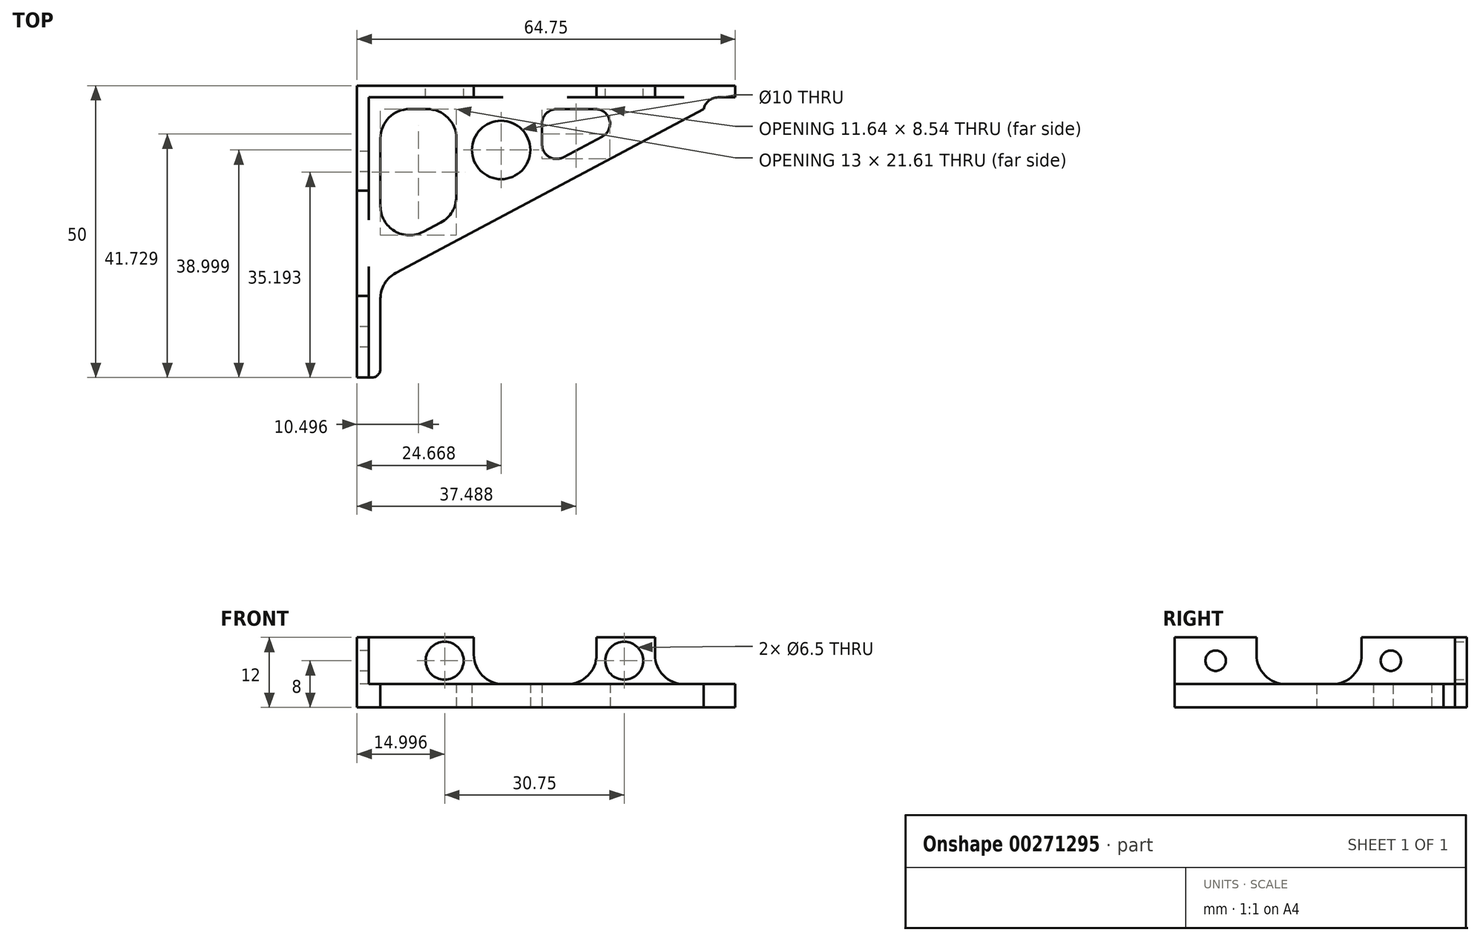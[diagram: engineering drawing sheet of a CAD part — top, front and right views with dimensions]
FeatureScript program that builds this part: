
annotation { "Feature Type Name" : "Feature", "Feature Type Description" : "" }
export const myFeature = defineFeature(function(context is Context, id is Id, definition is map)
    precondition{}
    {
        {
            var Q0;
            Q0=qCreatedBy(makeId("Top.planeOp"),FACE);
            var sketch = newSketch(context, id + "F0", { "sketchPlane" : qUnion([Q0])});
            skLineSegment(sketch, "E0.left", {"start": v(-24.04, 11.1) * mm, "end": v(-24.04, -13.83) * mm});
            skLineSegment(sketch, "E1", {"start": v(-28.04, 15.1) * mm, "end": v(-28.04, -34.9) * mm});
            skLineSegment(sketch, "E2", {"start": v(36.7, 15.1) * mm, "end": v(-28.04, 15.1) * mm});
            skLineSegment(sketch, "E3", {"start": v(-28.04, -34.9) * mm, "end": v(-24.04, -34.9) * mm});
            skLineSegment(sketch, "E4", {"start": v(-24.04, -34.9) * mm, "end": v(-24.04, -18.37) * mm});
            skLineSegment(sketch, "E5", {"start": v(-24.04, 11.1) * mm, "end": v(31.3, 11.1) * mm});
            skLineSegment(sketch, "E6", {"start": v(36.7, 15.1) * mm, "end": v(36.7, 13.1) * mm});
            skLineSegment(sketch, "E7", {"start": v(36.7, 13.1) * mm, "end": v(31.3, 13.1) * mm});
            skLineSegment(sketch, "E8", {"start": v(31.3, 13.1) * mm, "end": v(31.3, 11.1) * mm});
            skLineSegment(sketch, "E9", {"start": v(-24.04, -18.37) * mm, "end": v(31.3, 11.1) * mm});
            skLineSegment(sketch, "E10", {"start": v(-24.04, -13.83) * mm, "end": v(22.8, 11.1) * mm});
            skCircle(sketch, "E11", {"center": v(-3.37, 4.1) * mm, "radius": 5 * mm});
            skLineSegment(sketch, "E12", {"start": v(-11.04, 11.1) * mm, "end": v(-11.04, -6.91) * mm});
            skLineSegment(sketch, "E13", {"start": v(3.63, 11.1) * mm, "end": v(3.63, 0.9) * mm});
            skSolve(sketch);
        }
        {
            var Q0;
            {var subQ7=sQuery(id+"F0.wireOp",EDGE,"E0.left");Q0=makeQuery(id+"F0.imprint","IMPRINT",FACE,{"disambiguationData":[TD([[makeQuery(id+"F0.imprint","IMPRINT",EDGE,{"derivedFrom":subQ7}),-1.0]])]});}
            var Q1;
            Q1=makeQuery(id+"F0.imprint","IMPRINT",FACE,{"disambiguationData":[TD([[makeQuery(id+"F0.imprint","IMPRINT",EDGE,{"derivedFrom":sQuery(id+"F0.wireOp",EDGE,"E11")}),-1.0]])]});
            extrude(context, id + "F1", {"entities" : qUnion([Q0, Q1]), "depth" : 4 * mm});
        }
        {
            var Q0;
            Q0=qCreatedBy(makeId("Top.planeOp"),FACE);
            var sketch = newSketch(context, id + "F2", { "sketchPlane" : qUnion([Q0])});
            skLineSegment(sketch, "E14.bottom", {"start": v(-28.04, 15.1) * mm, "end": v(-26.04, 15.1) * mm});
            skLineSegment(sketch, "E14.top", {"start": v(-28.04, -2.9) * mm, "end": v(-26.04, -2.9) * mm});
            skLineSegment(sketch, "E14.left", {"start": v(-28.04, 15.1) * mm, "end": v(-28.04, -2.9) * mm});
            skLineSegment(sketch, "E14.right", {"start": v(-26.04, 15.1) * mm, "end": v(-26.04, -2.9) * mm});
            skLineSegment(sketch, "E15.bottom", {"start": v(-26.04, 13.1) * mm, "end": v(-8.04, 13.1) * mm});
            skLineSegment(sketch, "E15.top", {"start": v(-26.04, 15.1) * mm, "end": v(-8.04, 15.1) * mm});
            skLineSegment(sketch, "E15.left", {"start": v(-26.04, 13.1) * mm, "end": v(-26.04, 15.1) * mm});
            skLineSegment(sketch, "E15.right", {"start": v(-8.04, 13.1) * mm, "end": v(-8.04, 15.1) * mm});
            skLineSegment(sketch, "E16.bottom", {"start": v(-28.04, -34.9) * mm, "end": v(-26.04, -34.9) * mm});
            skLineSegment(sketch, "E16.top", {"start": v(-28.04, -20.9) * mm, "end": v(-26.04, -20.9) * mm});
            skLineSegment(sketch, "E16.left", {"start": v(-28.04, -34.9) * mm, "end": v(-28.04, -20.9) * mm});
            skLineSegment(sketch, "E16.right", {"start": v(-26.04, -34.9) * mm, "end": v(-26.04, -20.9) * mm});
            skLineSegment(sketch, "E17.bottom", {"start": v(12.96, 15.1) * mm, "end": v(22.96, 15.1) * mm});
            skLineSegment(sketch, "E17.top", {"start": v(12.96, 13.1) * mm, "end": v(22.96, 13.1) * mm});
            skLineSegment(sketch, "E17.left", {"start": v(12.96, 15.1) * mm, "end": v(12.96, 13.1) * mm});
            skLineSegment(sketch, "E17.right", {"start": v(22.96, 15.1) * mm, "end": v(22.96, 13.1) * mm});
            skSolve(sketch);
        }
        {
            var Q0;
            Q0=makeQuery(id+"F2.imprint","IMPRINT",FACE,{"disambiguationData":[TD([[makeQuery(id+"F2.imprint","IMPRINT",EDGE,{"derivedFrom":sQuery(id+"F2.wireOp",EDGE,"E17.bottom")}),-1.0]])]});
            var Q1;
            Q1=makeQuery(id+"F2.imprint","IMPRINT",FACE,{"disambiguationData":[TD([[makeQuery(id+"F2.imprint","IMPRINT",EDGE,{"derivedFrom":sQuery(id+"F2.wireOp",EDGE,"E15.bottom")}),1.0]])]});
            var Q2;
            Q2=makeQuery(id+"F2.imprint","IMPRINT",FACE,{"disambiguationData":[TD([[makeQuery(id+"F2.imprint","IMPRINT",EDGE,{"derivedFrom":sQuery(id+"F2.wireOp",EDGE,"E14.bottom")}),-1.0]])]});
            var Q3;
            Q3=makeQuery(id+"F2.imprint","IMPRINT",FACE,{"disambiguationData":[TD([[makeQuery(id+"F2.imprint","IMPRINT",EDGE,{"derivedFrom":sQuery(id+"F2.wireOp",EDGE,"E16.bottom")}),1.0]])]});
            extrude(context, id + "F3", {"entities" : qUnion([Q0, Q1, Q2, Q3]), "operationType" : NewBodyOperationType.ADD, "depth" : 12 * mm});
        }
        {
            var Q0;
            Q0=makeQuery(id+"F1.opExtrude","SWEPT_EDGE",EDGE,{"disambiguationData":[OSD([sQuery(id+"F0.wireOp",EDGE,"E0.left"),sQuery(id+"F0.wireOp",EDGE,"E5")])]});
            var Q1;
            Q1=makeQuery(id+"F1.opExtrude","SWEPT_EDGE",EDGE,{"disambiguationData":[OSD([sQuery(id+"F0.wireOp",EDGE,"E0.left"),sQuery(id+"F0.wireOp",EDGE,"E10")])]});
            var Q2;
            Q2=makeQuery(id+"F1.opExtrude","SWEPT_EDGE",EDGE,{"disambiguationData":[OSD([sQuery(id+"F0.wireOp",EDGE,"E10"),sQuery(id+"F0.wireOp",EDGE,"E12")])]});
            var Q3;
            Q3=makeQuery(id+"F1.opExtrude","SWEPT_EDGE",EDGE,{"disambiguationData":[OSD([sQuery(id+"F0.wireOp",EDGE,"E5"),sQuery(id+"F0.wireOp",EDGE,"E12")])]});
            var Q4;
            Q4=makeQuery(id+"F1.opExtrude","SWEPT_EDGE",EDGE,{"disambiguationData":[OSD([sQuery(id+"F0.wireOp",EDGE,"E4"),sQuery(id+"F0.wireOp",EDGE,"E9")])]});
            var Q5;
            Q5=makeQuery(id+"F3.boolean.opBoolean","INTERSECT",EDGE,{"derivedFrom":[makeQuery(id+"F1.opExtrude","CAP_FACE",FACE,{"disambiguationData":[OSD([sQuery(id+"F0.wireOp",EDGE,"E0.left"),sQuery(id+"F0.wireOp",EDGE,"E1"),sQuery(id+"F0.wireOp",EDGE,"E2"),sQuery(id+"F0.wireOp",EDGE,"E3"),sQuery(id+"F0.wireOp",EDGE,"E4"),sQuery(id+"F0.wireOp",EDGE,"E5"),sQuery(id+"F0.wireOp",EDGE,"E6"),sQuery(id+"F0.wireOp",EDGE,"E7"),sQuery(id+"F0.wireOp",EDGE,"E8"),sQuery(id+"F0.wireOp",EDGE,"E9"),sQuery(id+"F0.wireOp",EDGE,"E10"),sQuery(id+"F0.wireOp",EDGE,"E11"),sQuery(id+"F0.wireOp",EDGE,"E12"),sQuery(id+"F0.wireOp",EDGE,"E13")])],"isStart":false}),makeQuery(id+"F3.opExtrude","SWEPT_FACE",FACE,{"disambiguationData":[OSD([sQuery(id+"F2.wireOp",EDGE,"E14.top")])]})]});
            var Q6;
            Q6=makeQuery(id+"F3.boolean.opBoolean","INTERSECT",EDGE,{"derivedFrom":[makeQuery(id+"F1.opExtrude","CAP_FACE",FACE,{"disambiguationData":[OSD([sQuery(id+"F0.wireOp",EDGE,"E0.left"),sQuery(id+"F0.wireOp",EDGE,"E1"),sQuery(id+"F0.wireOp",EDGE,"E2"),sQuery(id+"F0.wireOp",EDGE,"E3"),sQuery(id+"F0.wireOp",EDGE,"E4"),sQuery(id+"F0.wireOp",EDGE,"E5"),sQuery(id+"F0.wireOp",EDGE,"E6"),sQuery(id+"F0.wireOp",EDGE,"E7"),sQuery(id+"F0.wireOp",EDGE,"E8"),sQuery(id+"F0.wireOp",EDGE,"E9"),sQuery(id+"F0.wireOp",EDGE,"E10"),sQuery(id+"F0.wireOp",EDGE,"E11"),sQuery(id+"F0.wireOp",EDGE,"E12"),sQuery(id+"F0.wireOp",EDGE,"E13")])],"isStart":false}),makeQuery(id+"F3.opExtrude","SWEPT_FACE",FACE,{"disambiguationData":[OSD([sQuery(id+"F2.wireOp",EDGE,"E16.top")])]})]});
            var Q7;
            Q7=makeQuery(id+"F3.boolean.opBoolean","INTERSECT",EDGE,{"derivedFrom":[makeQuery(id+"F1.opExtrude","CAP_FACE",FACE,{"disambiguationData":[OSD([sQuery(id+"F0.wireOp",EDGE,"E0.left"),sQuery(id+"F0.wireOp",EDGE,"E1"),sQuery(id+"F0.wireOp",EDGE,"E2"),sQuery(id+"F0.wireOp",EDGE,"E3"),sQuery(id+"F0.wireOp",EDGE,"E4"),sQuery(id+"F0.wireOp",EDGE,"E5"),sQuery(id+"F0.wireOp",EDGE,"E6"),sQuery(id+"F0.wireOp",EDGE,"E7"),sQuery(id+"F0.wireOp",EDGE,"E8"),sQuery(id+"F0.wireOp",EDGE,"E9"),sQuery(id+"F0.wireOp",EDGE,"E10"),sQuery(id+"F0.wireOp",EDGE,"E11"),sQuery(id+"F0.wireOp",EDGE,"E12"),sQuery(id+"F0.wireOp",EDGE,"E13")])],"isStart":false}),makeQuery(id+"F3.opExtrude","SWEPT_FACE",FACE,{"disambiguationData":[OSD([sQuery(id+"F2.wireOp",EDGE,"E15.right")])]})]});
            var Q8;
            Q8=makeQuery(id+"F3.boolean.opBoolean","INTERSECT",EDGE,{"derivedFrom":[makeQuery(id+"F1.opExtrude","CAP_FACE",FACE,{"disambiguationData":[OSD([sQuery(id+"F0.wireOp",EDGE,"E0.left"),sQuery(id+"F0.wireOp",EDGE,"E1"),sQuery(id+"F0.wireOp",EDGE,"E2"),sQuery(id+"F0.wireOp",EDGE,"E3"),sQuery(id+"F0.wireOp",EDGE,"E4"),sQuery(id+"F0.wireOp",EDGE,"E5"),sQuery(id+"F0.wireOp",EDGE,"E6"),sQuery(id+"F0.wireOp",EDGE,"E7"),sQuery(id+"F0.wireOp",EDGE,"E8"),sQuery(id+"F0.wireOp",EDGE,"E9"),sQuery(id+"F0.wireOp",EDGE,"E10"),sQuery(id+"F0.wireOp",EDGE,"E11"),sQuery(id+"F0.wireOp",EDGE,"E12"),sQuery(id+"F0.wireOp",EDGE,"E13")])],"isStart":false}),makeQuery(id+"F3.opExtrude","SWEPT_FACE",FACE,{"disambiguationData":[OSD([sQuery(id+"F2.wireOp",EDGE,"E17.left")])]})]});
            var Q9;
            Q9=makeQuery(id+"F3.boolean.opBoolean","INTERSECT",EDGE,{"derivedFrom":[makeQuery(id+"F1.opExtrude","CAP_FACE",FACE,{"disambiguationData":[OSD([sQuery(id+"F0.wireOp",EDGE,"E0.left"),sQuery(id+"F0.wireOp",EDGE,"E1"),sQuery(id+"F0.wireOp",EDGE,"E2"),sQuery(id+"F0.wireOp",EDGE,"E3"),sQuery(id+"F0.wireOp",EDGE,"E4"),sQuery(id+"F0.wireOp",EDGE,"E5"),sQuery(id+"F0.wireOp",EDGE,"E6"),sQuery(id+"F0.wireOp",EDGE,"E7"),sQuery(id+"F0.wireOp",EDGE,"E8"),sQuery(id+"F0.wireOp",EDGE,"E9"),sQuery(id+"F0.wireOp",EDGE,"E10"),sQuery(id+"F0.wireOp",EDGE,"E11"),sQuery(id+"F0.wireOp",EDGE,"E12"),sQuery(id+"F0.wireOp",EDGE,"E13")])],"isStart":false}),makeQuery(id+"F3.opExtrude","SWEPT_FACE",FACE,{"disambiguationData":[OSD([sQuery(id+"F2.wireOp",EDGE,"E17.right")])]})]});
            fillet(context, id + "F4", {"entities" : qUnion([Q0, Q1, Q2, Q3, Q4, Q5, Q6, Q7, Q8, Q9]), "radius" : 5 * mm, "tangentPropagation" : true, "allowEdgeOverflow" : false});
        }
        {
            var Q0;
            Q0=makeQuery(id+"F1.opExtrude","SWEPT_EDGE",EDGE,{"disambiguationData":[OSD([sQuery(id+"F0.wireOp",EDGE,"E7"),sQuery(id+"F0.wireOp",EDGE,"E8")])]});
            var Q1;
            Q1=makeQuery(id+"F1.opExtrude","SWEPT_EDGE",EDGE,{"disambiguationData":[OSD([sQuery(id+"F0.wireOp",EDGE,"E5"),sQuery(id+"F0.wireOp",EDGE,"E13")])]});
            var Q2;
            Q2=makeQuery(id+"F1.opExtrude","SWEPT_EDGE",EDGE,{"disambiguationData":[OSD([sQuery(id+"F0.wireOp",EDGE,"E10"),sQuery(id+"F0.wireOp",EDGE,"E13")])]});
            var Q3;
            Q3=makeQuery(id+"F1.opExtrude","SWEPT_EDGE",EDGE,{"disambiguationData":[OSD([sQuery(id+"F0.wireOp",EDGE,"E5"),sQuery(id+"F0.wireOp",EDGE,"E10")])]});
            fillet(context, id + "F5", {"entities" : qUnion([Q0, Q1, Q2, Q3]), "radius" : 2.5 * mm, "tangentPropagation" : true, "allowEdgeOverflow" : false});
        }
        {
            var Q0;
            Q0=makeQuery(id+"F1.opExtrude","SWEPT_EDGE",EDGE,{"disambiguationData":[OSD([sQuery(id+"F0.wireOp",EDGE,"E3"),sQuery(id+"F0.wireOp",EDGE,"E4")])]});
            fillet(context, id + "F6", {"entities" : qUnion([Q0]), "radius" : 1.5 * mm, "tangentPropagation" : true, "allowEdgeOverflow" : false});
        }
        {
            var Q0;
            Q0=makeQuery(id+"F3.boolean.opBoolean","MERGE",FACE,{"derivedFrom":[makeQuery(id+"F1.opExtrude","SWEPT_FACE",FACE,{"disambiguationData":[OSD([sQuery(id+"F0.wireOp",EDGE,"E2")])]}),makeQuery(id+"F3.opExtrude","SWEPT_FACE",FACE,{"disambiguationData":[OSD([sQuery(id+"F2.wireOp",EDGE,"E14.bottom"),sQuery(id+"F2.wireOp",EDGE,"E15.top")])]}),makeQuery(id+"F3.opExtrude","SWEPT_FACE",FACE,{"disambiguationData":[OSD([sQuery(id+"F2.wireOp",EDGE,"E17.bottom")])]})]});
            var sketch = newSketch(context, id + "F7", { "sketchPlane" : qUnion([Q0])});
            skCircle(sketch, "E18", {"center": v(-17.7, 8) * mm, "radius": 3.25 * mm});
            skCircle(sketch, "E19", {"center": v(13.04, 8) * mm, "radius": 3.25 * mm});
            skLineSegment(sketch, "E20", {"start": v(-5.9, 4) * mm, "end": v(-1.77, 4) * mm});
            skLineSegment(sketch, "E21", {"start": v(-5.05, 0) * mm, "end": v(-2.36, 0) * mm});
            skSolve(sketch);
        }
        {
            var Q0;
            Q0=makeQuery(id+"F3.boolean.opBoolean","MERGE",FACE,{"derivedFrom":[makeQuery(id+"F1.opExtrude","SWEPT_FACE",FACE,{"disambiguationData":[OSD([sQuery(id+"F0.wireOp",EDGE,"E1")])]}),makeQuery(id+"F3.opExtrude","SWEPT_FACE",FACE,{"disambiguationData":[OSD([sQuery(id+"F2.wireOp",EDGE,"E14.left")])]}),makeQuery(id+"F3.opExtrude","SWEPT_FACE",FACE,{"disambiguationData":[OSD([sQuery(id+"F2.wireOp",EDGE,"E16.left")])]})]});
            var sketch = newSketch(context, id + "F8", { "sketchPlane" : qUnion([Q0])});
            skCircle(sketch, "E22", {"center": v(-2.1, 8) * mm, "radius": 1.75 * mm});
            skCircle(sketch, "E23", {"center": v(27.9, 8) * mm, "radius": 1.75 * mm});
            skSolve(sketch);
        }
        {
            var Q0;
            Q0=makeQuery(id+"F7.imprint","IMPRINT",FACE,{"disambiguationData":[TD([[makeQuery(id+"F7.imprint","IMPRINT",EDGE,{"derivedFrom":sQuery(id+"F7.wireOp",EDGE,"E18")}),1.0]])]});
            var Q1;
            Q1=makeQuery(id+"F7.imprint","IMPRINT",FACE,{"disambiguationData":[TD([[makeQuery(id+"F7.imprint","IMPRINT",EDGE,{"derivedFrom":sQuery(id+"F7.wireOp",EDGE,"E19")}),1.0]])]});
            extrude(context, id + "F9", {"entities" : qUnion([Q0, Q1]), "operationType" : NewBodyOperationType.REMOVE, "oppositeDirection" : true, "depth" : 2 * mm});
        }
        {
            var Q0;
            Q0=makeQuery(id+"F8.imprint","IMPRINT",FACE,{"disambiguationData":[TD([[makeQuery(id+"F8.imprint","IMPRINT",EDGE,{"derivedFrom":sQuery(id+"F8.wireOp",EDGE,"E22")}),1.0]])]});
            var Q1;
            Q1=makeQuery(id+"F8.imprint","IMPRINT",FACE,{"disambiguationData":[TD([[makeQuery(id+"F8.imprint","IMPRINT",EDGE,{"derivedFrom":sQuery(id+"F8.wireOp",EDGE,"E23")}),1.0]])]});
            extrude(context, id + "F10", {"entities" : qUnion([Q0, Q1]), "operationType" : NewBodyOperationType.REMOVE, "oppositeDirection" : true, "depth" : 2 * mm});
        }
    });
